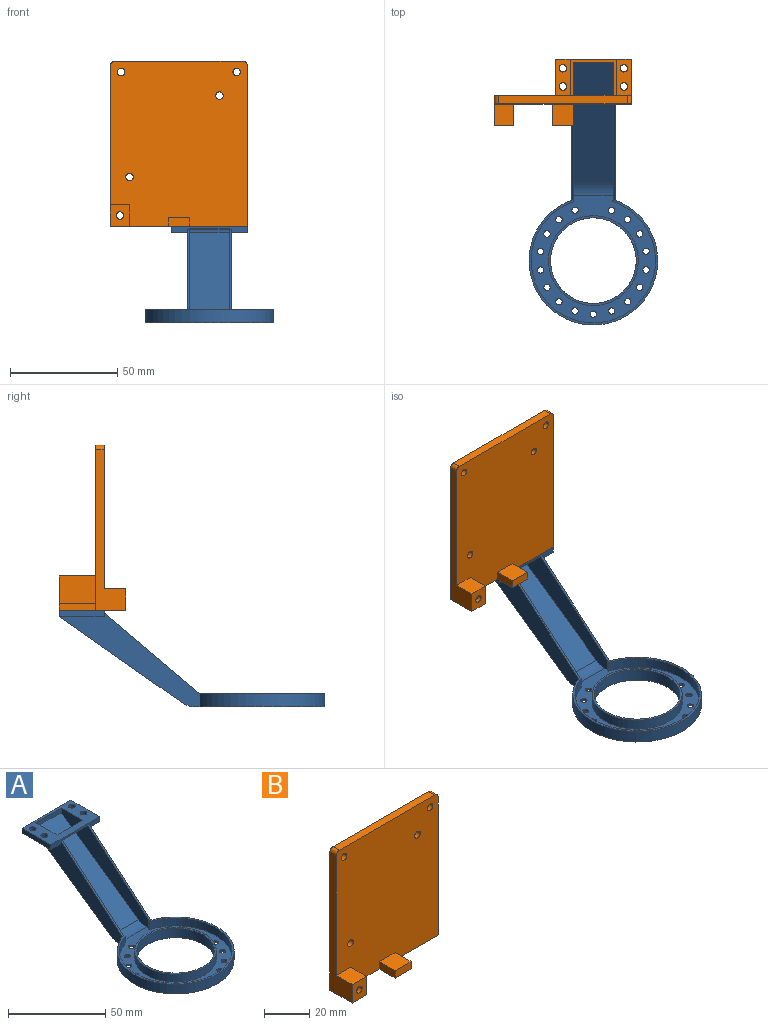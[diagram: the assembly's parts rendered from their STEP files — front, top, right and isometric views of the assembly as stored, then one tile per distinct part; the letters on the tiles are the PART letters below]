
ASSEMBLY  parts=2 mates=1
PART A: 52 faces, bbox 60.1x124x45 mm
  f0: plane 44.39x37.69mm, normal (0,-0.65,0.76), area 58.2mm2, adj f8,f13,f16,f44
  f1: plane 44.39x37.69mm, normal (0,-0.65,0.76), area 58.2mm2, adj f9,f15,f16,f44
  f2: plane 56.21x39.36mm, normal (0,-0.57,0.82), area 1269.6mm2, adj f8,f9,f19,f50
  f3: plane 57.4x40.19mm, normal (0,0.57,-0.82), area 1436.5mm2, adj f13,f15,f17,f51
  f4: cylinder r=30.05mm len=60.09mm, axis (0,0,-1), area 1007.2mm2, adj f13,f14,f15,f44
  f5: plane 5x0.55mm, normal (-1,0,0), area 2.7mm2, adj f10,f11,f12,f44
  f6: cylinder r=1.5mm len=3mm, axis (0,0,-1), area 9.4mm2, adj f11,f14
  f7: cylinder r=1.5mm len=3mm, axis (0,0,-1), area 9.4mm2, adj f11,f14
  f8: plane 64.97x44mm, normal (1,0,0), area 706.4mm2, adj f0,f2,f10,f11,f18,f19,f20,f25
  f9: plane 64.26x44mm, normal (-1,0,0), area 702.8mm2, adj f1,f2,f11,f12,f18,f19,f20,f25
  f10: cylinder r=29.05mm len=58.09mm, axis (0,0,-1), area 821mm2, adj f5,f8,f11,f44
  f11: plane 59.6x58.09mm, normal (0,0,1), area 1181.7mm2, adj f5,f6,f7,f8,f9,f10,f12,f28
  f12: plane 5x0.5mm, normal (0,1,0), area 2.5mm2, adj f5,f9,f11,f44
  f13: plane 65.76x43.69mm, normal (-1,0,0), area 726.4mm2, adj f0,f3,f4,f14,f16,f23,f44,f51
  f14: plane 60.91x60.09mm, normal (0,0,-1), area 1488.4mm2, adj f4,f6,f7,f13,f15,f27,f28,f30
  f15: plane 65.76x43.69mm, normal (1,0,0), area 726.4mm2, adj f1,f3,f4,f14,f16,f22,f44,f51
  f16: plane 35.5x3mm, normal (0,-1,0), area 71.9mm2, adj f0,f1,f13,f15,f21,f22,f23,f24
  f17: plane 35.5x3mm, normal (0,1,0), area 106.5mm2, adj f3,f21,f22,f23,f24,f26
  f18: plane 18.5x1mm, normal (0,1,0), area 18.5mm2, adj f8,f9,f20,f26
  f19: plane 18.5x2.83mm, normal (0,-1,0), area 52.3mm2, adj f2,f8,f9,f26
  f20: plane 18.5x3.63mm, normal (0,0,-1), area 67.2mm2, adj f8,f9,f18,f25
  f21: plane 21x3mm, normal (1,0,0), area 63mm2, adj f16,f17,f22,f26
  f22: plane 21x7.5mm, normal (0,0,-1), area 138.3mm2, adj f15,f16,f17,f21,f48,f49
  f23: plane 21x7.5mm, normal (0,0,-1), area 138.3mm2, adj f13,f16,f17,f24,f46,f47
  f24: plane 21x3mm, normal (-1,0,0), area 63mm2, adj f16,f17,f23,f26
  f25: plane 18.5x0.37mm, normal (0,0.65,-0.76), area 8.9mm2, adj f8,f9,f16,f20
  f26: plane 35.5x21mm, normal (0,0,1), area 420.3mm2, adj f8,f9,f16,f17,f18,f19,f21,f24
  f27: cylinder r=20mm len=40mm, axis (0,0,-1), area 754mm2, adj f14,f45
  f28: cylinder r=1.5mm len=3mm, axis (0,0,-1), area 9.4mm2, adj f11,f14
  f29: cylinder r=21mm len=42mm, axis (0,0,-1), area 659.7mm2, adj f11,f45
  f30: cylinder r=1.5mm len=3mm, axis (0,0,-1), area 9.4mm2, adj f11,f14
  f31: cylinder r=1.5mm len=3mm, axis (0,0,-1), area 9.4mm2, adj f11,f14
  f32: cylinder r=1.5mm len=3mm, axis (0,0,-1), area 9.4mm2, adj f11,f14
  f33: cylinder r=1.5mm len=3mm, axis (0,0,-1), area 9.4mm2, adj f11,f14
  f34: cylinder r=1.5mm len=3mm, axis (0,0,-1), area 9.4mm2, adj f11,f14
  f35: cylinder r=1.5mm len=3mm, axis (0,0,-1), area 9.4mm2, adj f11,f14
  f36: cylinder r=1.5mm len=3mm, axis (0,0,-1), area 9.4mm2, adj f11,f14
  f37: cylinder r=1.5mm len=3mm, axis (0,0,-1), area 9.4mm2, adj f11,f14
  f38: cylinder r=1.5mm len=3mm, axis (0,0,-1), area 9.4mm2, adj f11,f14
  f39: cylinder r=1.5mm len=3mm, axis (0,0,-1), area 9.4mm2, adj f11,f14
  f40: cylinder r=1.5mm len=3mm, axis (0,0,-1), area 9.4mm2, adj f11,f14
  f41: cylinder r=1.5mm len=3mm, axis (0,0,-1), area 9.4mm2, adj f11,f14
  f42: cylinder r=1.5mm len=3mm, axis (0,0,-1), area 9.4mm2, adj f11,f14
  f43: cylinder r=1.5mm len=3mm, axis (0,0,-1), area 9.4mm2, adj f11,f14
  f44: plane 60.09x58.66mm, normal (0,0,1), area 167.5mm2, adj f0,f1,f4,f5,f8,f9,f10,f12
  f45: plane 42x42mm, normal (0,0,1), area 128.8mm2, adj f27,f29
  f46: cylinder r=1.75mm len=3.5mm, axis (0,0,-1), area 33mm2, adj f23,f26
  f47: cylinder r=1.75mm len=3.5mm, axis (0,0,-1), area 33mm2, adj f23,f26
  f48: cylinder r=1.75mm len=3.5mm, axis (0,0,-1), area 33mm2, adj f22,f26
  f49: cylinder r=1.75mm len=3.5mm, axis (0,0,-1), area 33mm2, adj f22,f26
  f50: cylinder r=10mm len=18.5mm, axis (1,0,0), area 113mm2, adj f2,f8,f9,f11
  f51: cylinder r=10mm len=20.5mm, axis (1,0,0), area 125.2mm2, adj f3,f13,f14,f15
PART B: 39 faces, bbox 64x31x77 mm
  f0: cylinder r=1.75mm len=3.5mm, axis (0,1,0), area 22mm2, adj f31,f36
  f1: plane 77x64mm, normal (0,1,0), area 4764.8mm2, adj f2,f4,f5,f6,f7,f8,f9,f14
  f2: plane 17x13mm, normal (1,0,0), area 221mm2, adj f1,f17,f18,f22
  f3: plane 77x64mm, normal (0,-1,0), area 4757.8mm2, adj f4,f5,f6,f7,f8,f9,f10,f11
  f4: plane 60x4mm, normal (0,0,1), area 240mm2, adj f1,f3,f37,f38
  f5: plane 75x14mm, normal (-1,0,0), area 400mm2, adj f1,f3,f6,f30,f31,f37
  f6: plane 64x31mm, normal (0,0,-1), area 724.3mm2, adj f1,f3,f5,f7,f10,f12,f13,f18
  f7: plane 75x21mm, normal (1,0,0), area 351mm2, adj f1,f3,f6,f18,f22,f38
  f8: cylinder r=1.75mm len=4mm, axis (0,-1,0), area 44mm2, adj f1,f3
  f9: cylinder r=1.75mm len=4mm, axis (0,-1,0), area 44mm2, adj f1,f3
  f10: plane 10x4mm, normal (1,0,0), area 40mm2, adj f3,f6,f11,f13
  f11: plane 10x10mm, normal (0,0,1), area 100mm2, adj f3,f10,f12,f13
  f12: plane 10x4mm, normal (-1,0,0), area 40mm2, adj f3,f6,f11,f13
  f13: plane 10x4mm, normal (0,-1,0), area 40mm2, adj f6,f10,f11,f12
  f14: cylinder r=1.75mm len=4mm, axis (0,-1,0), area 44mm2, adj f1,f3
  f15: cylinder r=1.75mm len=4mm, axis (0,-1,0), area 44mm2, adj f1,f3
  f16: plane 17x13mm, normal (-1,0,0), area 221mm2, adj f1,f17,f18,f23
  f17: plane 21.5x17mm, normal (0,0,1), area 78.8mm2, adj f1,f2,f16,f18,f19,f20,f21
  f18: plane 35.5x16mm, normal (0,1,0), area 386mm2, adj f2,f6,f7,f16,f17,f22,f23,f24
  f19: plane 16x15.5mm, normal (-1,0,0), area 248mm2, adj f1,f6,f17,f21
  f20: plane 16x15.5mm, normal (1,0,0), area 248mm2, adj f1,f6,f17,f21
  f21: plane 18.5x16mm, normal (0,-1,0), area 296mm2, adj f6,f17,f19,f20
  f22: plane 17x7mm, normal (0,0,1), area 99.8mm2, adj f1,f2,f7,f18,f27,f28
  f23: plane 17x7mm, normal (0,0,1), area 99.8mm2, adj f1,f16,f18,f24,f25,f26
  f24: plane 17x3mm, normal (-1,0,0), area 51mm2, adj f1,f6,f18,f23
  f25: cylinder r=1.75mm len=3.5mm, axis (0,0,1), area 33mm2, adj f6,f23
  f26: cylinder r=1.75mm len=3.5mm, axis (0,0,1), area 33mm2, adj f6,f23
  f27: cylinder r=1.75mm len=3.5mm, axis (0,0,1), area 33mm2, adj f6,f22
  f28: cylinder r=1.75mm len=3.5mm, axis (0,0,1), area 33mm2, adj f6,f22
  f29: plane 10x10mm, normal (1,0,0), area 100mm2, adj f3,f6,f30,f31
  f30: plane 10x9mm, normal (0,0,1), area 90mm2, adj f3,f5,f29,f31
  f31: plane 10x9mm, normal (0,-1,0), area 80.4mm2, adj f0,f5,f6,f29,f30
  f32: plane 12x6mm, normal (-1,0,0), area 72mm2, adj f1,f33,f35,f36
  f33: plane 12x5.5mm, normal (0,0,1), area 66mm2, adj f1,f32,f34,f36
  f34: plane 12x6mm, normal (1,0,0), area 72mm2, adj f1,f33,f35,f36
  f35: plane 12x5.5mm, normal (0,0,-1), area 66mm2, adj f1,f32,f34,f36
  f36: plane 6x5.5mm, normal (0,1,0), area 23.4mm2, adj f0,f32,f33,f34,f35
  f37: cylinder r=2mm len=4mm, axis (0,-1,0), area 12.6mm2, adj f1,f3,f4,f5
  f38: cylinder r=2mm len=4mm, axis (0,1,0), area 12.6mm2, adj f1,f3,f4,f7
PLACE A t=(2.08,24.81,-49.28)mm
PLACE B t=(-1.92,101.81,34.22)mm
MATE fastened B.f6 <-> A.f26  axis (0,0,-1) through (30.08,97.81,-4.28)mm
